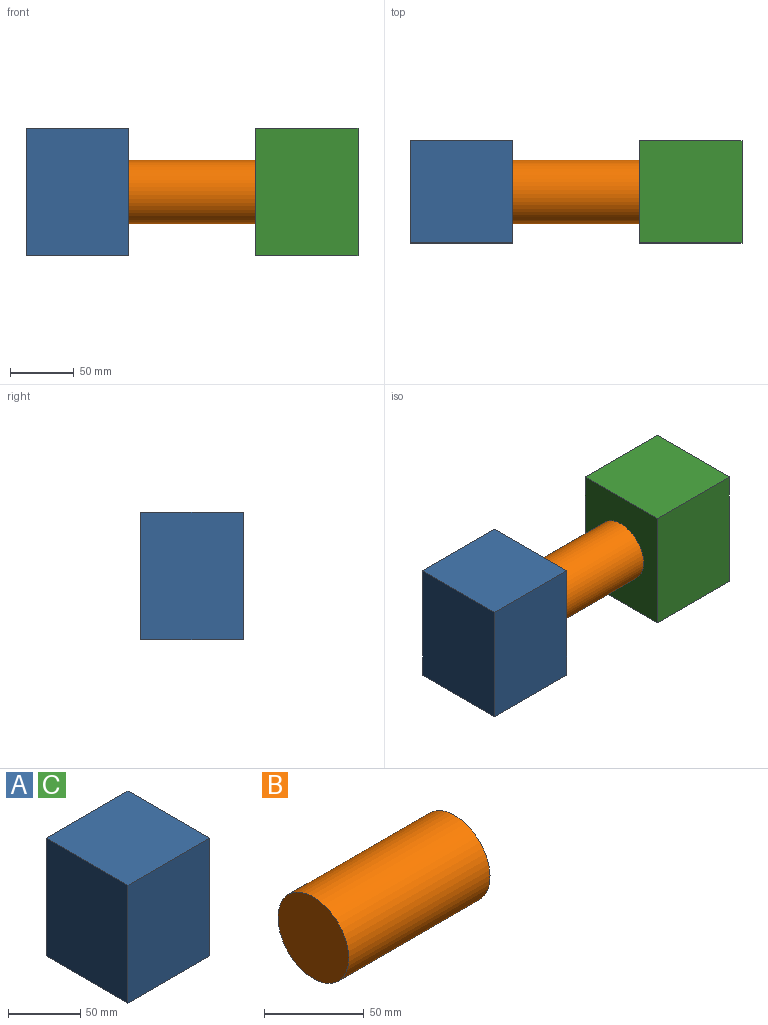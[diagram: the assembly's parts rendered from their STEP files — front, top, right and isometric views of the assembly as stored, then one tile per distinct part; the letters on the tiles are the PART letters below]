
ASSEMBLY  parts=3 mates=2
PART A: 6 faces, bbox 80x80x100 mm
  f0: plane 100x80mm, normal (-1,0,0), area 8000mm2, adj f1,f3,f4,f5
  f1: plane 100x80mm, normal (0,-1,0), area 8000mm2, adj f0,f2,f4,f5
  f2: plane 100x80mm, normal (1,0,0), area 8000mm2, adj f1,f3,f4,f5
  f3: plane 100x80mm, normal (0,1,0), area 8000mm2, adj f0,f2,f4,f5
  f4: plane 80x80mm, normal (0,0,1), area 6400mm2, adj f0,f1,f2,f3
  f5: plane 80x80mm, normal (0,0,-1), area 6400mm2, adj f0,f1,f2,f3
PART B: 3 faces, bbox 100x50x50 mm
  f0: cylinder r=25mm len=100mm, axis (-1,0,0), area 15708mm2, adj f1,f2
  f1: plane 50x50mm, normal (1,0,0), area 1963.5mm2, adj f0
  f2: plane 50x50mm, normal (-1,0,0), area 1963.5mm2, adj f0
PART C: same geometry as A
PLACE A t=(-180,0,-25)mm
PLACE B at identity fixed
PLACE C t=(0,0,-25)mm
MATE slider A.f2 <-> B.f0  axis (1,0,0) through (-50,0,25)mm
MATE slider C.f0 <-> B.f0  axis (-1,0,0) through (50,0,25)mm
